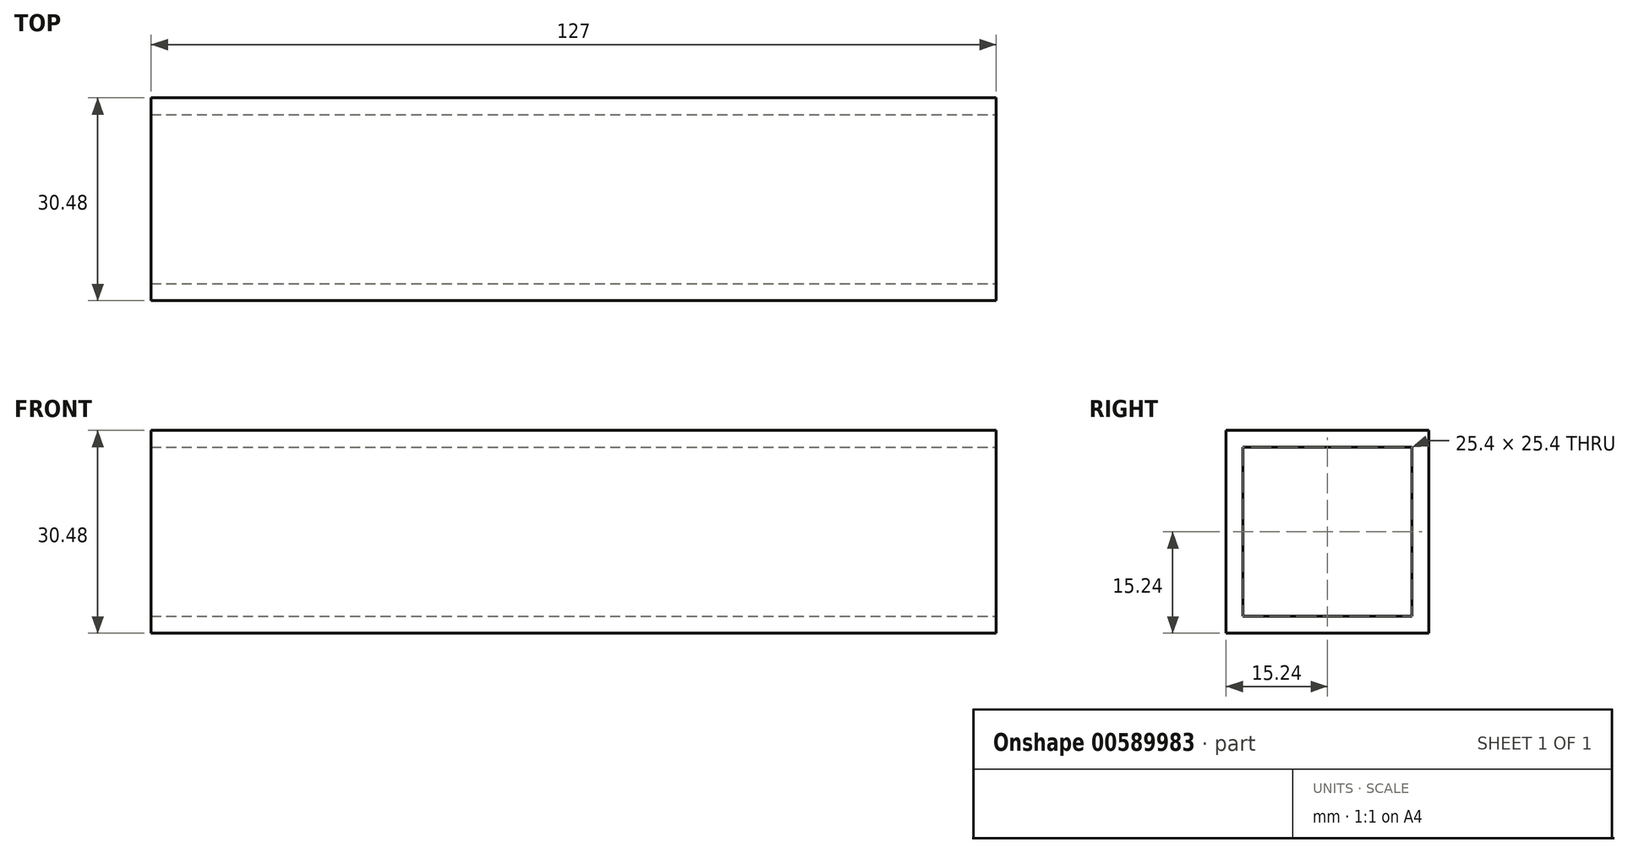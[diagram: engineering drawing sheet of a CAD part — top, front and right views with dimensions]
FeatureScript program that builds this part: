
annotation { "Feature Type Name" : "Feature", "Feature Type Description" : "" }
export const myFeature = defineFeature(function(context is Context, id is Id, definition is map)
    precondition{}
    {
        {
            var Q0;
            Q0=qCreatedBy(makeId("Right.planeOp"),FACE);
            var sketch = newSketch(context, id + "F0", { "sketchPlane" : qUnion([Q0])});
            skLineSegment(sketch, "E0.bottom", {"start": v(0, 0) * mm, "end": v(30.48, 0) * mm});
            skLineSegment(sketch, "E0.top", {"start": v(0, 30.48) * mm, "end": v(30.48, 30.48) * mm});
            skLineSegment(sketch, "E0.left", {"start": v(0, 0) * mm, "end": v(0, 30.48) * mm});
            skLineSegment(sketch, "E0.right", {"start": v(30.48, 0) * mm, "end": v(30.48, 30.48) * mm});
            skSolve(sketch);
        }
        {
            var Q0;
            Q0 = qSketchRegion(id + "F0", true);
            extrude(context, id + "F1", {"entities" : qUnion([Q0]), "oppositeDirection" : true, "depth" : 127 * mm, "offsetDistance" : 25.4 * mm});
        }
        {
            var Q0;
            Q0=makeQuery(id+"F1.opExtrude","CAP_FACE",FACE,{"disambiguationData":[OSD([sQuery(id+"F0.wireOp",EDGE,"E0.bottom"),sQuery(id+"F0.wireOp",EDGE,"E0.top"),sQuery(id+"F0.wireOp",EDGE,"E0.left"),sQuery(id+"F0.wireOp",EDGE,"E0.right")])],"isStart":true});
            var sketch = newSketch(context, id + "F2", { "sketchPlane" : qUnion([Q0])});
            skLineSegment(sketch, "E1.bottom", {"start": v(27.94, 27.94) * mm, "end": v(2.54, 27.94) * mm});
            skLineSegment(sketch, "E1.top", {"start": v(27.94, 2.54) * mm, "end": v(2.54, 2.54) * mm});
            skLineSegment(sketch, "E1.left", {"start": v(27.94, 27.94) * mm, "end": v(27.94, 2.54) * mm});
            skLineSegment(sketch, "E1.right", {"start": v(2.54, 27.94) * mm, "end": v(2.54, 2.54) * mm});
            skPoint(sketch, "E1.middle", {"position": v(15.24, 15.24) * mm});
            skPoint(sketch, "E1.middle.positionSnap0", {"position": v(15.24, 30.48) * mm});
            skPoint(sketch, "E1.middle.positionSnap1", {"position": v(30.48, 15.24) * mm});
            skPoint(sketch, "E1.centerSnap0", {"position": v(15.24, 30.48) * mm});
            skPoint(sketch, "E1.centerSnap1", {"position": v(30.48, 15.24) * mm});
            skSolve(sketch);
        }
        {
            var Q0;
            Q0 = qSketchRegion(id + "F2", true);
            extrude(context, id + "F3", {"entities" : qUnion([Q0]), "operationType" : NewBodyOperationType.REMOVE, "oppositeDirection" : true, "depth" : 127 * mm, "offsetDistance" : 25.4 * mm});
        }
    });
